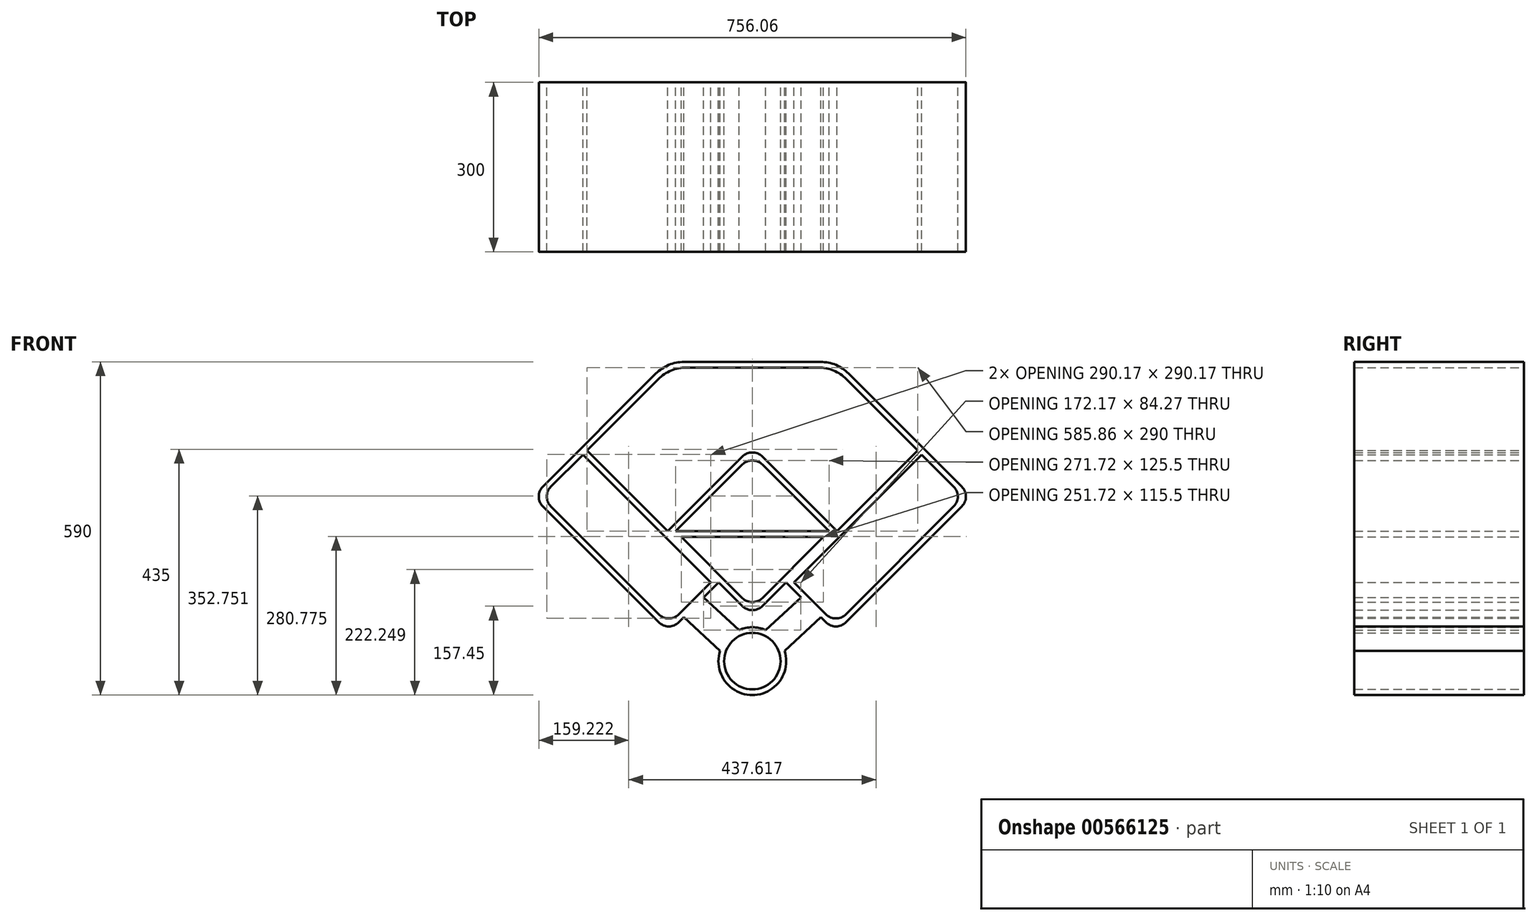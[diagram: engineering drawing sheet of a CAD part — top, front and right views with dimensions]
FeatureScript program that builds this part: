
annotation { "Feature Type Name" : "Feature", "Feature Type Description" : "" }
export const myFeature = defineFeature(function(context is Context, id is Id, definition is map)
    precondition{}
    {
        {
            var Q0;
            Q0=qCreatedBy(makeId("Front.planeOp"),FACE);
            var sketch = newSketch(context, id + "F0", { "sketchPlane" : qUnion([Q0])});
            skLineSegment(sketch, "E0", {"start": v(-300, 0) * mm, "end": v(-170.5, 129.5) * mm});
            skLineSegment(sketch, "E1", {"start": v(170.5, 129.5) * mm, "end": v(300, 0) * mm});
            skLineSegment(sketch, "E2", {"start": v(150, -150) * mm, "end": v(17.68, -282.32) * mm});
            skLineSegment(sketch, "E3", {"start": v(-17.68, -282.32) * mm, "end": v(-150, -150) * mm});
            skPoint(sketch, "E4.endSnap0", {"position": v(150, 150) * mm});
            skLineSegment(sketch, "E5.0", {"start": v(-17.68, -268.18) * mm, "end": v(-135.86, -150) * mm});
            skLineSegment(sketch, "E5.1", {"start": v(135.86, -150) * mm, "end": v(17.68, -268.18) * mm});
            skLineSegment(sketch, "E6.0", {"start": v(-67.93, -82.07) * mm, "end": v(-135.86, -150) * mm});
            skLineSegment(sketch, "E6.1", {"start": v(-67.93, -82.07) * mm, "end": v(-17.68, -31.82) * mm});
            skLineSegment(sketch, "E6.2", {"start": v(67.93, -82.07) * mm, "end": v(17.68, -31.82) * mm});
            skLineSegment(sketch, "E6.3", {"start": v(67.93, -82.07) * mm, "end": v(135.86, -150) * mm});
            skLineSegment(sketch, "E7", {"start": v(-150, -150) * mm, "end": v(-17.68, -17.68) * mm});
            skLineSegment(sketch, "E8", {"start": v(17.68, -17.68) * mm, "end": v(150, -150) * mm});
            skPoint(sketch, "E9.orphan", {"position": v(0, 300) * mm});
            skLineSegment(sketch, "E10", {"start": v(-121, 150) * mm, "end": v(121, 150) * mm});
            skLineSegment(sketch, "E11.1", {"start": v(-285.86, 0) * mm, "end": v(-166.36, 119.5) * mm});
            skLineSegment(sketch, "E11.3", {"start": v(-116.86, 140) * mm, "end": v(116.86, 140) * mm});
            skLineSegment(sketch, "E11.7", {"start": v(166.36, 119.5) * mm, "end": v(285.86, 0) * mm});
            skLineSegment(sketch, "E12", {"start": v(-300, 0) * mm, "end": v(-370.71, -70.71) * mm});
            skLineSegment(sketch, "E13", {"start": v(-370.71, -106.07) * mm, "end": v(-165.65, -311.13) * mm});
            skLineSegment(sketch, "E14", {"start": v(-130.3, -311.13) * mm, "end": v(-59.58, -240.42) * mm});
            skLineSegment(sketch, "E15.0", {"start": v(-300, -14.14) * mm, "end": v(-73.73, -240.42) * mm});
            skLineSegment(sketch, "E15.1", {"start": v(-300, -14.14) * mm, "end": v(-356.57, -70.71) * mm});
            skLineSegment(sketch, "E15.2", {"start": v(-356.57, -106.07) * mm, "end": v(-165.65, -296.98) * mm});
            skLineSegment(sketch, "E15.3", {"start": v(-130.3, -296.98) * mm, "end": v(-73.73, -240.42) * mm});
            skLineSegment(sketch, "E16", {"start": v(-300, 0) * mm, "end": v(-150, -150) * mm});
            skLineSegment(sketch, "E17", {"start": v(300, 0) * mm, "end": v(370.71, -70.71) * mm});
            skLineSegment(sketch, "E18", {"start": v(370.71, -106.07) * mm, "end": v(165.65, -311.13) * mm});
            skLineSegment(sketch, "E19", {"start": v(130.3, -311.13) * mm, "end": v(59.58, -240.42) * mm});
            skLineSegment(sketch, "E20.0", {"start": v(73.73, -240.42) * mm, "end": v(300, -14.14) * mm});
            skLineSegment(sketch, "E20.1", {"start": v(130.3, -296.98) * mm, "end": v(73.73, -240.42) * mm});
            skLineSegment(sketch, "E20.2", {"start": v(356.57, -106.07) * mm, "end": v(165.65, -296.98) * mm});
            skLineSegment(sketch, "E20.3", {"start": v(300, -14.14) * mm, "end": v(356.57, -70.71) * mm});
            skCircle(sketch, "E21", {"center": v(-150, 0) * mm, "radius": 65 * mm});
            skCircle(sketch, "E22", {"center": v(150, 0) * mm, "radius": 65 * mm});
            skCircle(sketch, "E23", {"center": v(0, -380) * mm, "radius": 50 * mm});
            skLineSegment(sketch, "E24", {"start": v(-57.08, -361.5) * mm, "end": v(-121.47, -302.3) * mm});
            skLineSegment(sketch, "E25", {"start": v(-23.24, -324.68) * mm, "end": v(-86.08, -266.92) * mm});
            skLineSegment(sketch, "E26", {"start": v(57.08, -361.5) * mm, "end": v(121.47, -302.3) * mm});
            skLineSegment(sketch, "E27", {"start": v(23.24, -324.68) * mm, "end": v(86.08, -266.92) * mm});
            skPoint(sketch, "E28.end.orphan", {"position": v(-103.78, -284.61) * mm});
            skCircle(sketch, "E29.0", {"center": v(0, -380) * mm, "radius": 60 * mm});
            skLineSegment(sketch, "E30", {"start": v(-135.86, -150) * mm, "end": v(135.86, -150) * mm});
            skLineSegment(sketch, "E31.0", {"start": v(-125.86, -160) * mm, "end": v(125.86, -160) * mm});
            skPoint(sketch, "E32.visualSharp", {"position": v(-145.86, 140) * mm});
            skArc(sketch, "E32.filletArc", {"start": v(-116.86, 140) * mm, "mid": v(-143.65, 134.67) * mm, "end": v(-166.36, 119.5) * mm});
            skPoint(sketch, "E33.visualSharp", {"position": v(-150, 150) * mm});
            skArc(sketch, "E33.filletArc", {"start": v(-121, 150) * mm, "mid": v(-147.8, 144.67) * mm, "end": v(-170.5, 129.5) * mm});
            skPoint(sketch, "E34.visualSharp", {"position": v(145.86, 140) * mm});
            skArc(sketch, "E34.filletArc", {"start": v(166.36, 119.5) * mm, "mid": v(143.65, 134.67) * mm, "end": v(116.86, 140) * mm});
            skArc(sketch, "E35.filletArc", {"start": v(170.5, 129.5) * mm, "mid": v(147.8, 144.67) * mm, "end": v(121, 150) * mm});
            skPoint(sketch, "E36.visualSharp", {"position": v(-147.97, -328.8) * mm});
            skArc(sketch, "E36.filletArc", {"start": v(-165.65, -311.13) * mm, "mid": v(-147.97, -318.45) * mm, "end": v(-130.3, -311.13) * mm});
            skPoint(sketch, "E37.visualSharp", {"position": v(-147.97, -314.66) * mm});
            skArc(sketch, "E37.filletArc", {"start": v(-165.65, -296.98) * mm, "mid": v(-147.97, -304.3) * mm, "end": v(-130.3, -296.98) * mm});
            skPoint(sketch, "E38.visualSharp", {"position": v(-374.25, -88.39) * mm});
            skArc(sketch, "E38.filletArc", {"start": v(-356.57, -70.71) * mm, "mid": v(-363.9, -88.39) * mm, "end": v(-356.57, -106.07) * mm});
            skPoint(sketch, "E39.visualSharp", {"position": v(-388.39, -88.39) * mm});
            skArc(sketch, "E39.filletArc", {"start": v(-370.71, -70.71) * mm, "mid": v(-378.03, -88.39) * mm, "end": v(-370.71, -106.07) * mm});
            skPoint(sketch, "E40.visualSharp", {"position": v(147.97, -328.8) * mm});
            skArc(sketch, "E40.filletArc", {"start": v(130.3, -311.13) * mm, "mid": v(147.97, -318.45) * mm, "end": v(165.65, -311.13) * mm});
            skPoint(sketch, "E41.visualSharp", {"position": v(147.97, -314.66) * mm});
            skArc(sketch, "E41.filletArc", {"start": v(130.3, -296.98) * mm, "mid": v(147.97, -304.3) * mm, "end": v(165.65, -296.98) * mm});
            skPoint(sketch, "E42.visualSharp", {"position": v(374.25, -88.39) * mm});
            skArc(sketch, "E42.filletArc", {"start": v(356.57, -106.07) * mm, "mid": v(363.9, -88.39) * mm, "end": v(356.57, -70.71) * mm});
            skPoint(sketch, "E43.visualSharp", {"position": v(388.39, -88.39) * mm});
            skArc(sketch, "E43.filletArc", {"start": v(370.71, -106.07) * mm, "mid": v(378.03, -88.39) * mm, "end": v(370.71, -70.71) * mm});
            skPoint(sketch, "E44.visualSharp", {"position": v(0, 14.14) * mm});
            skPoint(sketch, "E45.visualSharp", {"position": v(0, -300) * mm});
            skArc(sketch, "E45.filletArc", {"start": v(-17.68, -282.32) * mm, "mid": v(0, -289.64) * mm, "end": v(17.68, -282.32) * mm});
            skPoint(sketch, "E46.visualSharp", {"position": v(0, -285.86) * mm});
            skArc(sketch, "E46.filletArc", {"start": v(-17.68, -268.18) * mm, "mid": v(0, -275.5) * mm, "end": v(17.68, -268.18) * mm});
            skPoint(sketch, "E47.visualSharp", {"position": v(0, -14.14) * mm});
            skArc(sketch, "E47.filletArc", {"start": v(17.68, -31.82) * mm, "mid": v(0, -24.5) * mm, "end": v(-17.68, -31.82) * mm});
            skPoint(sketch, "E48.visualSharp", {"position": v(0, 0) * mm});
            skArc(sketch, "E48.filletArc", {"start": v(17.68, -17.68) * mm, "mid": v(0, -10.36) * mm, "end": v(-17.68, -17.68) * mm});
            skLineSegment(sketch, "E49", {"start": v(-285.86, 0) * mm, "end": v(-292.93, -7.07) * mm});
            skLineSegment(sketch, "E50", {"start": v(285.86, 0) * mm, "end": v(300, -14.14) * mm});
            skLineSegment(sketch, "E51", {"start": v(150, -150) * mm, "end": v(292.93, -7.07) * mm});
            skSolve(sketch);
        }
        {
            var Q0;
            Q0=makeQuery(id+"F0.imprint","IMPRINT",FACE,{"disambiguationData":[TD([[makeQuery(id+"F0.imprint","IMPRINT",EDGE,{"derivedFrom":sQuery(id+"F0.wireOp",EDGE,"E0")}),-1.0]])]});
            var Q1;
            {var subQ0=sQuery(id+"F0.wireOp",EDGE,"E30");Q1=makeQuery(id+"F0.imprint","IMPRINT",FACE,{"disambiguationData":[TD([[makeQuery(id+"F0.imprint","IMPRINT",EDGE,{"derivedFrom":subQ0}),-1.0]])]});}
            var Q2;
            Q2=makeQuery(id+"F0.imprint","IMPRINT",FACE,{"disambiguationData":[TD([[makeQuery(id+"F0.imprint","IMPRINT",EDGE,{"derivedFrom":sQuery(id+"F0.wireOp",EDGE,"E12")}),1.0]])]});
            var Q3;
            {var subQ5=sQuery(id+"F0.wireOp",EDGE,"qQ9FKNjt-qgQu-uNXr-7irZ-RsSz2cuaI32E");Q3=makeQuery(id+"F0.imprint","IMPRINT",FACE,{"disambiguationData":[TD([[makeQuery(id+"F0.imprint","IMPRINT",EDGE,{"derivedFrom":subQ5}),1.0]])]});}
            var Q4;
            Q4=makeQuery(id+"F0.imprint","IMPRINT",FACE,{"disambiguationData":[TD([[makeQuery(id+"F0.imprint","IMPRINT",EDGE,{"derivedFrom":sQuery(id+"F0.wireOp",EDGE,"E23")}),-1.0]])]});
            var Q5;
            {var subQ0=sQuery(id+"F0.wireOp",EDGE,"E26");Q5=makeQuery(id+"F0.imprint","IMPRINT",FACE,{"disambiguationData":[TD([[makeQuery(id+"F0.imprint","IMPRINT",EDGE,{"derivedFrom":subQ0}),1.0]])]});}
            var Q6;
            {var subQ0=sQuery(id+"F0.wireOp",EDGE,"E24");Q6=makeQuery(id+"F0.imprint","IMPRINT",FACE,{"disambiguationData":[TD([[makeQuery(id+"F0.imprint","IMPRINT",EDGE,{"derivedFrom":subQ0}),-1.0]])]});}
            var Q7;
            {var subQ0=sQuery(id+"F0.wireOp",EDGE,"E6.0");Q7=makeQuery(id+"F0.imprint","IMPRINT",FACE,{"disambiguationData":[TD([[makeQuery(id+"F0.imprint","IMPRINT",EDGE,{"derivedFrom":subQ0}),-1.0]])]});}
            extrude(context, id + "F1", {"entities" : qUnion([Q0, Q1, Q2, Q3, Q4, Q5, Q6, Q7]), "endBound" : BoundingType.SYMMETRIC, "depth" : 300 * mm, "offsetDistance" : 25 * mm});
        }
    });
